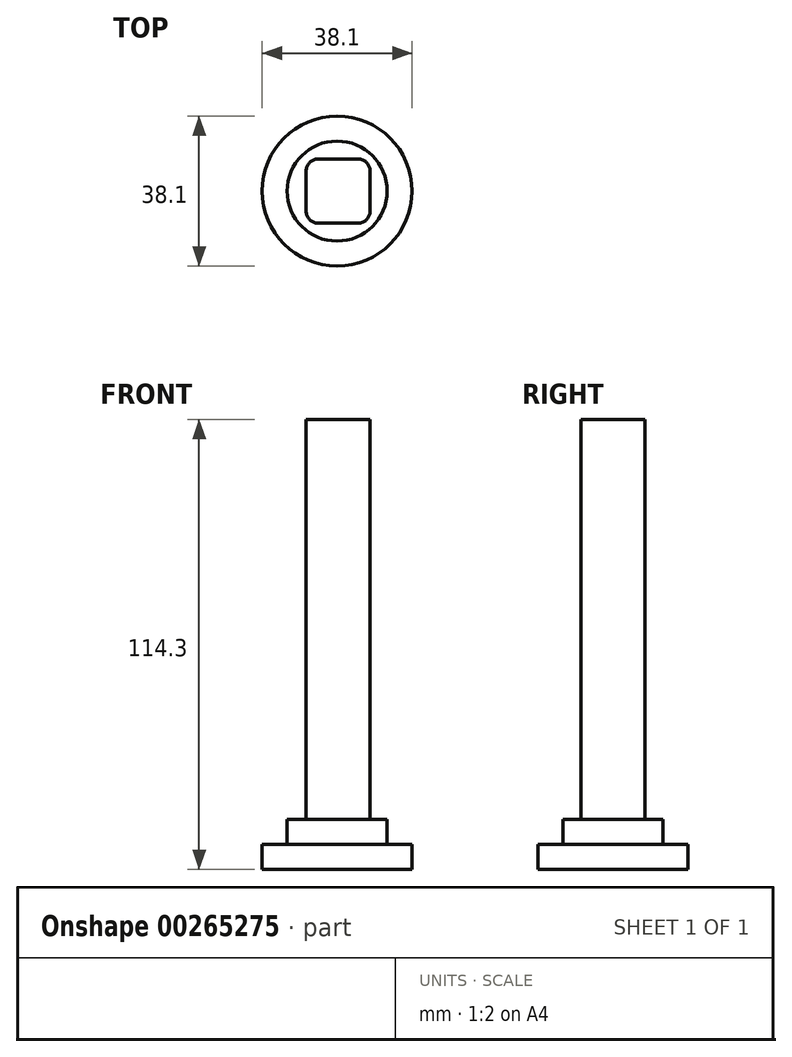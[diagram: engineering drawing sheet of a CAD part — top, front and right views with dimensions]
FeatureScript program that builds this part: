
annotation { "Feature Type Name" : "Feature", "Feature Type Description" : "" }
export const myFeature = defineFeature(function(context is Context, id is Id, definition is map)
    precondition{}
    {
        {
            var Q0;
            Q0=qCreatedBy(makeId("Top.planeOp"),FACE);
            var sketch = newSketch(context, id + "F0", { "sketchPlane" : qUnion([Q0])});
            skLineSegment(sketch, "E0.bottom", {"start": v(0, 0) * mm, "end": v(16.26, 0) * mm});
            skLineSegment(sketch, "E0.top", {"start": v(0, 16.26) * mm, "end": v(16.26, 16.26) * mm});
            skLineSegment(sketch, "E0.left", {"start": v(0, 0) * mm, "end": v(0, 16.26) * mm});
            skLineSegment(sketch, "E0.right", {"start": v(16.26, 0) * mm, "end": v(16.26, 16.26) * mm});
            skLineSegment(sketch, "E1.bottom", {"start": v(-4.83, -4.57) * mm, "end": v(20.57, -4.57) * mm});
            skLineSegment(sketch, "E1.top", {"start": v(-4.83, 20.83) * mm, "end": v(20.57, 20.83) * mm});
            skLineSegment(sketch, "E1.left", {"start": v(-4.83, -4.57) * mm, "end": v(-4.83, 20.83) * mm});
            skLineSegment(sketch, "E1.right", {"start": v(20.57, -4.57) * mm, "end": v(20.57, 20.83) * mm});
            skLineSegment(sketch, "E2", {"start": v(7.87, 16.26) * mm, "end": v(7.87, 20.83) * mm, "construction": true});
            skPoint(sketch, "E2.startSnap0", {"position": v(7.87, 20.83) * mm});
            skLineSegment(sketch, "E3", {"start": v(8.13, 0) * mm, "end": v(8.13, -4.57) * mm, "construction": true});
            skLineSegment(sketch, "E4.bottom", {"start": v(-11.18, -10.92) * mm, "end": v(26.92, -10.92) * mm});
            skLineSegment(sketch, "E4.top", {"start": v(-11.18, 27.18) * mm, "end": v(26.92, 27.18) * mm});
            skLineSegment(sketch, "E4.left", {"start": v(-11.18, -10.92) * mm, "end": v(-11.18, 27.18) * mm});
            skLineSegment(sketch, "E4.right", {"start": v(26.92, -10.92) * mm, "end": v(26.92, 27.18) * mm});
            skLineSegment(sketch, "E5", {"start": v(7.87, 20.83) * mm, "end": v(7.87, 27.18) * mm, "construction": true});
            skLineSegment(sketch, "E6", {"start": v(-4.83, 8.13) * mm, "end": v(-11.18, 8.13) * mm, "construction": true});
            skSolve(sketch);
        }
        {
            var Q0;
            Q0=makeQuery(id+"F0.imprint","IMPRINT",FACE,{"disambiguationData":[TD([[makeQuery(id+"F0.imprint","IMPRINT",EDGE,{"derivedFrom":sQuery(id+"F0.wireOp",EDGE,"E0.bottom")}),1.0]])]});
            extrude(context, id + "F1", {"entities" : qUnion([Q0]), "depth" : 114.3 * mm});
        }
        {
            var Q0;
            Q0=makeQuery(id+"F0.imprint","IMPRINT",FACE,{"disambiguationData":[TD([[makeQuery(id+"F0.imprint","IMPRINT",EDGE,{"derivedFrom":sQuery(id+"F0.wireOp",EDGE,"E0.bottom")}),-1.0]])]});
            extrude(context, id + "F2", {"entities" : qUnion([Q0]), "operationType" : NewBodyOperationType.ADD, "depth" : 12.7 * mm});
        }
        {
            var Q0;
            Q0=makeQuery(id+"F1.opExtrude","SWEPT_EDGE",EDGE,{"disambiguationData":[OSD([sQuery(id+"F0.wireOp",EDGE,"E0.top"),sQuery(id+"F0.wireOp",EDGE,"E0.left")])]});
            var Q1;
            Q1=makeQuery(id+"F1.opExtrude","SWEPT_EDGE",EDGE,{"disambiguationData":[OSD([sQuery(id+"F0.wireOp",EDGE,"E0.top"),sQuery(id+"F0.wireOp",EDGE,"E0.right")])]});
            var Q2;
            Q2=makeQuery(id+"F1.opExtrude","SWEPT_EDGE",EDGE,{"disambiguationData":[OSD([sQuery(id+"F0.wireOp",EDGE,"E0.bottom"),sQuery(id+"F0.wireOp",EDGE,"E0.right")])]});
            var Q3;
            Q3=makeQuery(id+"F1.opExtrude","SWEPT_EDGE",EDGE,{"disambiguationData":[OSD([sQuery(id+"F0.wireOp",EDGE,"E0.bottom"),sQuery(id+"F0.wireOp",EDGE,"E0.left")])]});
            fillet(context, id + "F3", {"entities" : qUnion([Q0, Q1, Q2, Q3]), "radius" : 3.05 * mm, "tangentPropagation" : true, "allowEdgeOverflow" : false});
        }
        {
            var Q0;
            Q0=makeQuery(id+"F2.opExtrude","SWEPT_EDGE",EDGE,{"disambiguationData":[OSD([sQuery(id+"F0.wireOp",EDGE,"E1.top"),sQuery(id+"F0.wireOp",EDGE,"E1.left")])]});
            var Q1;
            Q1=makeQuery(id+"F2.opExtrude","SWEPT_EDGE",EDGE,{"disambiguationData":[OSD([sQuery(id+"F0.wireOp",EDGE,"E1.bottom"),sQuery(id+"F0.wireOp",EDGE,"E1.left")])]});
            var Q2;
            Q2=makeQuery(id+"F2.opExtrude","SWEPT_EDGE",EDGE,{"disambiguationData":[OSD([sQuery(id+"F0.wireOp",EDGE,"E1.bottom"),sQuery(id+"F0.wireOp",EDGE,"E1.right")])]});
            var Q3;
            Q3=makeQuery(id+"F2.opExtrude","SWEPT_EDGE",EDGE,{"disambiguationData":[OSD([sQuery(id+"F0.wireOp",EDGE,"E1.top"),sQuery(id+"F0.wireOp",EDGE,"E1.right")])]});
            fillet(context, id + "F4", {"entities" : qUnion([Q0, Q1, Q2, Q3]), "radius" : 12.7 * mm, "tangentPropagation" : true, "allowEdgeOverflow" : false});
        }
        {
            var Q0;
            Q0=makeQuery(id+"F0.imprint","IMPRINT",FACE,{"disambiguationData":[TD([[makeQuery(id+"F0.imprint","IMPRINT",EDGE,{"derivedFrom":sQuery(id+"F0.wireOp",EDGE,"E1.bottom")}),-1.0]])]});
            var Q1;
            Q1=makeQuery(id+"F0.imprint","IMPRINT",FACE,{"disambiguationData":[TD([[makeQuery(id+"F0.imprint","IMPRINT",EDGE,{"derivedFrom":sQuery(id+"F0.wireOp",EDGE,"E0.bottom")}),-1.0]])]});
            extrude(context, id + "F5", {"entities" : qUnion([Q0, Q1]), "operationType" : NewBodyOperationType.ADD, "depth" : 6.35 * mm});
        }
        {
            var Q0;
            Q0=makeQuery(id+"F5.opExtrude","SWEPT_EDGE",EDGE,{"disambiguationData":[OSD([sQuery(id+"F0.wireOp",EDGE,"E4.top"),sQuery(id+"F0.wireOp",EDGE,"E4.left")])]});
            var Q1;
            Q1=makeQuery(id+"F5.opExtrude","SWEPT_EDGE",EDGE,{"disambiguationData":[OSD([sQuery(id+"F0.wireOp",EDGE,"E4.top"),sQuery(id+"F0.wireOp",EDGE,"E4.right")])]});
            var Q2;
            Q2=makeQuery(id+"F5.opExtrude","SWEPT_EDGE",EDGE,{"disambiguationData":[OSD([sQuery(id+"F0.wireOp",EDGE,"E4.bottom"),sQuery(id+"F0.wireOp",EDGE,"E4.right")])]});
            var Q3;
            Q3=makeQuery(id+"F5.opExtrude","SWEPT_EDGE",EDGE,{"disambiguationData":[OSD([sQuery(id+"F0.wireOp",EDGE,"E4.bottom"),sQuery(id+"F0.wireOp",EDGE,"E4.left")])]});
            fillet(context, id + "F6", {"entities" : qUnion([Q0, Q1, Q2, Q3]), "radius" : 19.05 * mm, "tangentPropagation" : true, "allowEdgeOverflow" : false});
        }
    });
